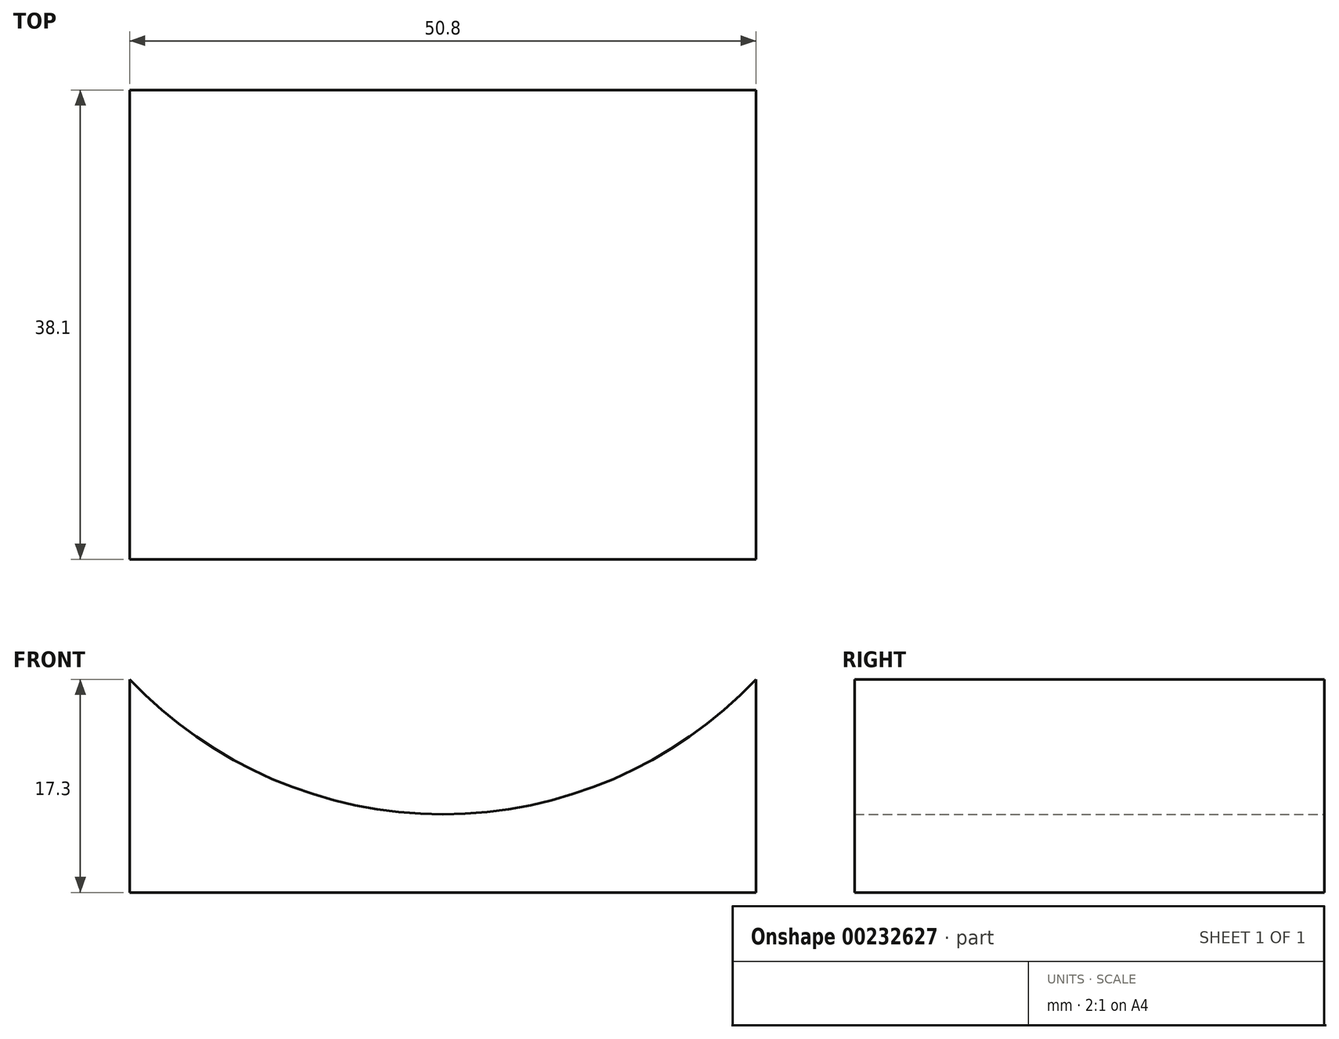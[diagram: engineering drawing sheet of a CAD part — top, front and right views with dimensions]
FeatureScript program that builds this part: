
annotation { "Feature Type Name" : "Feature", "Feature Type Description" : "" }
export const myFeature = defineFeature(function(context is Context, id is Id, definition is map)
    precondition{}
    {
        {
            var Q0;
            Q0=qCreatedBy(makeId("Front.planeOp"),FACE);
            var sketch = newSketch(context, id + "F0", { "sketchPlane" : qUnion([Q0])});
            skLineSegment(sketch, "E0", {"start": v(0, 0) * mm, "end": v(50.8, 0) * mm});
            skLineSegment(sketch, "E1", {"start": v(25.4, 0) * mm, "end": v(25.4, 6.35) * mm});
            skArc(sketch, "E2", {"start": v(0, 17.3) * mm, "mid": v(25.4, 6.35) * mm, "end": v(50.8, 17.3) * mm});
            skLineSegment(sketch, "E3", {"start": v(50.8, 0) * mm, "end": v(50.8, 17.3) * mm});
            skLineSegment(sketch, "E4", {"start": v(0, 17.3) * mm, "end": v(0, 0) * mm});
            skSolve(sketch);
        }
        {
            var Q0;
            Q0 = qSketchRegion(id + "F0", true);
            extrude(context, id + "F1", {"entities" : qUnion([Q0]), "depth" : 38.1 * mm});
        }
    });
